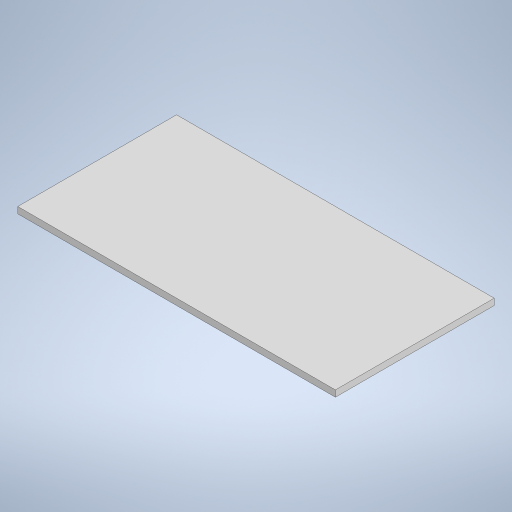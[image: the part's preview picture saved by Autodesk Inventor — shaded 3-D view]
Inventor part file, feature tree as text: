
AUTODESK INVENTOR PART (.ipt)
format: ipt  version: 2024 (Build 280153000, 153)  size: 204,800 bytes
history: native  units: mm
features: extrude x1, sketch x1
ambient origin geometry x8: Origin, YZ Plane, XZ Plane, XY Plane, X Axis, Y Axis, Z Axis, Center Point
bodies: Solid1 (feature_tree)
feature tree (2):
  extrude  "Extrusion1"  Depth=50.0mm
  sketch  "Sketch1"  dims[d0=100.0mm d1=50.0mm d2=2.0mm d3=0.0mm]
